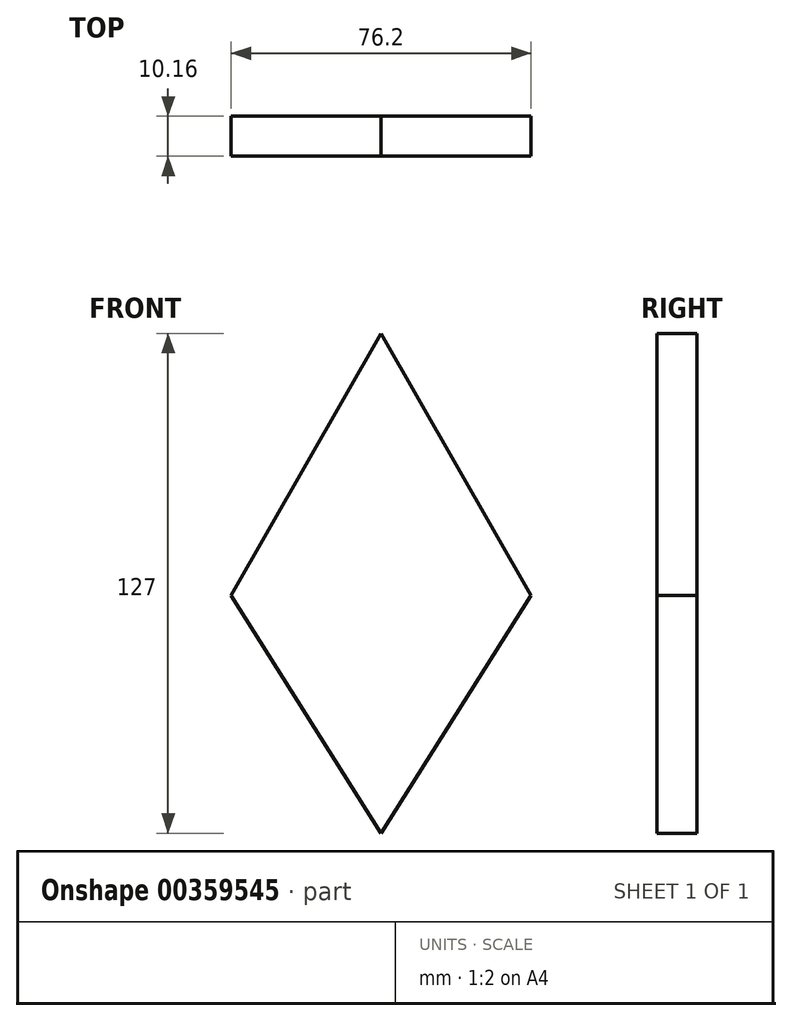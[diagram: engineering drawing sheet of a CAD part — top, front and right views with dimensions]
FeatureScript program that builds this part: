
annotation { "Feature Type Name" : "Feature", "Feature Type Description" : "" }
export const myFeature = defineFeature(function(context is Context, id is Id, definition is map)
    precondition{}
    {
        {
            var Q0;
            Q0=qCreatedBy(makeId("Front.planeOp"),FACE);
            var sketch = newSketch(context, id + "F0", { "sketchPlane" : qUnion([Q0])});
            skPoint(sketch, "E0.middle", {"position": v(0, 0) * mm});
            skLineSegment(sketch, "E1", {"start": v(0, 66.62) * mm, "end": v(38.1, 0) * mm});
            skLineSegment(sketch, "E2", {"start": v(38.1, 0) * mm, "end": v(0, -60.38) * mm});
            skLineSegment(sketch, "E3.MirrorCS", {"start": v(0, 66.62) * mm, "end": v(-38.1, 0) * mm});
            skLineSegment(sketch, "E4.MirrorCS", {"start": v(-38.1, 0) * mm, "end": v(0, -60.38) * mm});
            skSolve(sketch);
        }
        {
            var Q0;
            Q0=makeQuery(id+"F0.imprint","IMPRINT",FACE,{"disambiguationData":[TD([[makeQuery(id+"F0.imprint","IMPRINT",EDGE,{"derivedFrom":sQuery(id+"F0.wireOp",EDGE,"E1")}),-1.0]])]});
            extrude(context, id + "F1", {"entities" : qUnion([Q0]), "depth" : 10.16 * mm});
        }
    });
